# Revit family: EZTA+NO HWC
name_source: partatom
category: Mechanical Equipment
revit_build: Autodesk Revit 2018 (Build: 20170223_1515(x64)
units: mm (PartAtom-declared; Revit-internal decimal feet)

## family parameters
Always vertical = Yes
Cut with Voids When Loaded = No
OmniClass Number = 23.75.00.00
OmniClass Title = Climate Control (HVAC)
Part Type = Normal
Room Calculation Point = No
Round Connector Dimension = Use Diameter
Shared = No
Work Plane-Based = No

## types (24) — shared parameters
Discharge = 0' - 0 5/8"
EnclosureFront = 0' - 3"
EnclosureHeight = 0' - 11 3/32"
EnclosureWidth = 0' - 7 1/8"
EnslosureRear = 1' - 2 7/32"
Inlet_S = 0' - 5 3/8"
Length = 3' - 3 1/2"
Manufacturer = ANEMOSTAT PRODUCTS
Model = EZTA+
Overlap = 0' - 0 5/8"
URL = https://www.anemostat-hvac.com

## per-type parameters (varying)
| type | Coil | Description | DischargeX | DischargeY | EnclosureCenter | Height | InletDia | InletRadius | LeftController | Power Left Controller | Power Right Controller | RightController | SlipDrive | Width |
| EZTA+0508 W/LH Controller | 0' - 3 3/4" | EZTA+ W/Integral Sound Attenuator | 0' - 10 3/4" | 0' - 8 3/4" | 0' - 5" | 0' - 10" | 0' - 4 7/8" | 0' - 2 7/16" | Yes | Yes | No | No | 3' - 7 1/4" | 1' - 0" |
| EZTA+0608 W/LH Controller | 0' - 3 3/4" | EZTA+ W/Integral Sound Attenuator | 0' - 10 3/4" | 0' - 8 3/4" | 0' - 5" | 0' - 10" | 0' - 5 7/8" | 0' - 2 15/16" | Yes | Yes | No | No | 3' - 7 1/4" | 1' - 0" |
| EZTA+0508 W/RH Controller | 0' - 3 3/4" | EZTA W/Integral Sound Attenuator | 0' - 10 3/4" | 0' - 8 3/4" | 0' - 5" | 0' - 10" | 0' - 4 7/8" | 0' - 2 7/16" | No | No | Yes | Yes | 3' - 7 1/4" | 1' - 0" |
| EZTA+0608 W/RH Controller | 0' - 3 3/4" | EZTA+ W/Integral Sound Attenuator | 0' - 10 3/4" | 0' - 8 3/4" | 0' - 5" | 0' - 10" | 0' - 5 7/8" | 0' - 2 15/16" | No | No | Yes | Yes | 3' - 7 1/4" | 1' - 0" |
| EZTA+0508 NO Controller | 0' - 3 3/4" | EZTA+ W/Integral Sound Attenuator | 0' - 10 3/4" | 0' - 8 3/4" | 0' - 5" | 0' - 10" | 0' - 4 7/8" | 0' - 2 7/16" | No | No | No | No | 3' - 7 1/4" | 1' - 0" |
| EZTA+0608 NO Controller | 0' - 3 3/4" | EZTA+ W/Integral Sound Attenuator | 0' - 10 3/4" | 0' - 8 3/4" | 0' - 5" | 0' - 10" | 0' - 5 7/8" | 0' - 2 15/16" | No | No | No | No | 3' - 7 1/4" | 1' - 0" |
| EZTA+0710 W/LH Controller | 0' - 6 15/16" | EZTA+ W/Integral Sound Attenuator | 1' - 0 3/4" | 0' - 11 1/4" | 0' - 6 1/4" | 1' - 0 1/2" | 0' - 6 7/8" | 0' - 3 7/16" | Yes | Yes | No | No | 3' - 10 7/16" | 1' - 2" |
| EZTA+0810 W/LH Controller | 0' - 6 15/16" | EZTA+ W/Integral Sound Attenuator | 1' - 0 3/4" | 0' - 11 1/4" | 0' - 6 1/4" | 1' - 0 1/2" | 0' - 7 7/8" | 0' - 3 15/16" | Yes | Yes | No | No | 3' - 10 7/16" | 1' - 2" |
| EZTA+0710 W/RH Controller | 0' - 6 15/16" | EZTA+ W/Integral Sound Attenuator | 1' - 0 3/4" | 0' - 11 1/4" | 0' - 6 1/4" | 1' - 0 1/2" | 0' - 6 7/8" | 0' - 3 7/16" | No | No | Yes | Yes | 3' - 10 7/16" | 1' - 2" |
| EZTA+0810 W/RH Controller | 0' - 6 15/16" | EZTA+ W/Integral Sound Attenuator | 1' - 0 3/4" | 0' - 11 1/4" | 0' - 6 1/4" | 1' - 0 1/2" | 0' - 7 7/8" | 0' - 3 15/16" | No | No | Yes | Yes | 3' - 10 7/16" | 1' - 2" |
| EZTA+0810 NO Controller | 0' - 6 15/16" | EZTA+ W/Integral Sound Attenuator | 1' - 0 3/4" | 0' - 11 1/4" | 0' - 6 1/4" | 1' - 0 1/2" | 0' - 7 7/8" | 0' - 3 15/16" | No | No | No | No | 3' - 10 7/16" | 1' - 2" |
| EZTA+0710 NO Controller | 0' - 6 15/16" | EZTA+ W/Integral Sound Attenuator | 1' - 0 3/4" | 0' - 11 1/4" | 0' - 6 1/4" | 1' - 0 1/2" | 0' - 6 7/8" | 0' - 3 7/16" | No | No | No | No | 3' - 10 7/16" | 1' - 2" |
| EZTA+1012 W/LH Controller | 0' - 3 3/4" | EZTA+ W/Integral Sound Attenuator | 1' - 2 3/4" | 1' - 1 3/4" | 0' - 7 1/2" | 1' - 3" | 0' - 9 7/8" | 0' - 4 15/16" | Yes | Yes | No | No | 3' - 7 1/4" | 1' - 4" |
| EZTA+1012 NO Controller | 0' - 3 3/4" | EZTA+ W/Integral Sound Attenuator | 1' - 2 3/4" | 1' - 1 3/4" | 0' - 7 1/2" | 1' - 3" | 0' - 9 7/8" | 0' - 4 15/16" | No | No | No | No | 3' - 7 1/4" | 1' - 4" |
| EZTA+0912 NO Controller | 0' - 3 3/4" | EZTA+ W/Integral Sound Attenuator | 1' - 2 3/4" | 1' - 1 3/4" | 0' - 7 1/2" | 1' - 3" | 0' - 8 7/8" | 0' - 4 7/16" | No | No | No | No | 3' - 7 1/4" | 1' - 4" |
| EZTA+0912 W/LH Controller | 0' - 3 3/4" | EZTA+ W/Integral Sound Attenuator | 1' - 2 3/4" | 1' - 1 3/4" | 0' - 7 1/2" | 1' - 3" | 0' - 8 7/8" | 0' - 4 7/16" | Yes | Yes | No | No | 3' - 7 1/4" | 1' - 4" |
| EZTA+0912 W/RH Controller | 0' - 3 3/4" | EZTA+ W/Integral Sound Attenuator | 1' - 2 3/4" | 1' - 1 3/4" | 0' - 7 1/2" | 1' - 3" | 0' - 8 7/8" | 0' - 4 7/16" | No | No | Yes | Yes | 3' - 7 1/4" | 1' - 4" |
| EZTA+1012 W/RH Controller | 0' - 3 3/4" | EZTA+ W/Integral Sound Attenuator | 1' - 2 3/4" | 1' - 1 3/4" | 0' - 7 1/2" | 1' - 3" | 0' - 9 7/8" | 0' - 4 15/16" | No | No | Yes | Yes | 3' - 7 1/4" | 1' - 4" |
| EZTA+1214 W/LH Controller | 0' - 3 3/4" | EZTA+ W/Integral Sound Attenuator | 1' - 6 3/4" | 1' - 4 1/4" | 0' - 8 3/4" | 1' - 5 1/2" | 0' - 11 7/8" | 0' - 5 15/16" | Yes | Yes | No | No | 3' - 7 1/4" | 1' - 8" |
| EZTA+1214 W/RH Controller | 0' - 3 3/4" | EZTA+ W/Integral Sound Attenuator | 1' - 6 3/4" | 1' - 4 1/4" | 0' - 8 3/4" | 1' - 5 1/2" | 0' - 11 7/8" | 0' - 5 15/16" | No | No | Yes | Yes | 3' - 7 1/4" | 1' - 8" |
| EZTA+1214 NO Controller | 0' - 3 3/4" | EZTA+ W/Integral Sound Attenuator | 1' - 6 3/4" | 1' - 4 1/4" | 0' - 8 3/4" | 1' - 5 1/2" | 0' - 11 7/8" | 0' - 5 15/16" | No | No | No | No | 3' - 7 1/4" | 1' - 8" |
| EZTA+1416 W/LH Controller | 0' - 4 15/16" | EZTA+ W/Integral Sound Attenuator | 1' - 10 3/4" | 1' - 4 1/4" | 0' - 8 3/4" | 1' - 5 1/2" | 1' - 1 7/8" | 0' - 6 15/16" | Yes | Yes | No | No | 3' - 8 7/16" | 2' - 0" |
| EZTA+1416 W/RH Controller | 0' - 4 15/16" | EZTA+ W/Integral Sound Attenuator | 1' - 10 3/4" | 1' - 4 1/4" | 0' - 8 3/4" | 1' - 5 1/2" | 1' - 1 7/8" | 0' - 6 15/16" | No | No | Yes | Yes | 3' - 8 7/16" | 2' - 0" |
| EZTA+1416 NO Controller | 0' - 4 15/16" | EZTA+ W/Integral Sound Attenuator | 1' - 10 3/4" | 1' - 4 1/4" | 0' - 8 3/4" | 1' - 5 1/2" | 1' - 1 7/8" | 0' - 6 15/16" | No | No | No | No | 3' - 8 7/16" | 2' - 0" |

## geometry (parser evidence)
native form markers: Sweep x2
no freeform markers — native parametric forms only
